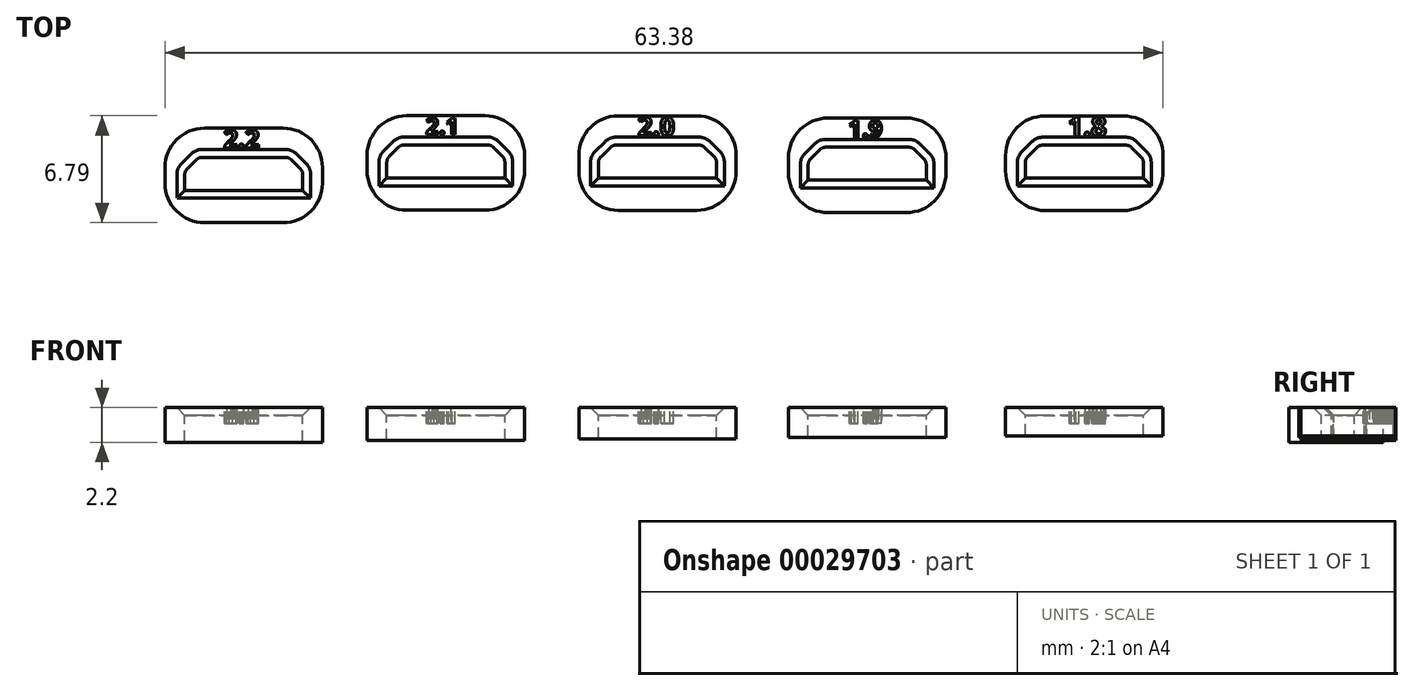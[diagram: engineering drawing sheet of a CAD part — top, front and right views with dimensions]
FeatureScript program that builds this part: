
annotation { "Feature Type Name" : "Feature", "Feature Type Description" : "" }
export const myFeature = defineFeature(function(context is Context, id is Id, definition is map)
    precondition{}
    {
        {
            var Q0;
            Q0=qCreatedBy(makeId("Top.planeOp"),FACE);
            var sketch = newSketch(context, id + "F0", { "sketchPlane" : qUnion([Q0])});
            skLineSegment(sketch, "E0", {"start": v(-1.37, -1.33) * mm, "end": v(6.13, -1.33) * mm});
            skLineSegment(sketch, "E1", {"start": v(6.13, -1.33) * mm, "end": v(6.13, -0.13) * mm});
            skLineSegment(sketch, "E2", {"start": v(6.13, -0.13) * mm, "end": v(5.23, 0.77) * mm});
            skLineSegment(sketch, "E3", {"start": v(5.23, 0.77) * mm, "end": v(-0.47, 0.77) * mm});
            skLineSegment(sketch, "E4", {"start": v(-0.47, 0.77) * mm, "end": v(-1.37, -0.13) * mm});
            skLineSegment(sketch, "E5", {"start": v(-1.37, -0.13) * mm, "end": v(-1.37, -1.33) * mm});
            skLineSegment(sketch, "E6.bottom", {"start": v(-2.62, 2.62) * mm, "end": v(7.38, 2.62) * mm});
            skLineSegment(sketch, "E6.top", {"start": v(-2.62, -3.38) * mm, "end": v(7.38, -3.38) * mm});
            skLineSegment(sketch, "E6.left", {"start": v(-2.62, 2.62) * mm, "end": v(-2.62, -3.38) * mm});
            skLineSegment(sketch, "E6.right", {"start": v(7.38, 2.62) * mm, "end": v(7.38, -3.38) * mm});
            skSolve(sketch);
        }
        {
            var Q0;
            Q0=makeQuery(id+"F0.imprint","IMPRINT",FACE,{"disambiguationData":[TD([[makeQuery(id+"F0.imprint","IMPRINT",EDGE,{"derivedFrom":sQuery(id+"F0.wireOp",EDGE,"E0")}),-1.0]])]});
            extrude(context, id + "F1", {"entities" : qUnion([Q0]), "oppositeDirection" : true, "depth" : 2.2 * mm});
        }
        {
            var Q0;
            Q0=qCreatedBy(makeId("Top.planeOp"),FACE);
            var sketch = newSketch(context, id + "F2", { "sketchPlane" : qUnion([Q0])});
            skLineSegment(sketch, "E7", {"start": v(11.46, -0.54) * mm, "end": v(18.96, -0.54) * mm});
            skLineSegment(sketch, "E8", {"start": v(18.96, -0.54) * mm, "end": v(18.96, 0.66) * mm});
            skLineSegment(sketch, "E9", {"start": v(18.96, 0.66) * mm, "end": v(18.06, 1.56) * mm});
            skLineSegment(sketch, "E10", {"start": v(18.06, 1.56) * mm, "end": v(12.36, 1.56) * mm});
            skLineSegment(sketch, "E11", {"start": v(12.36, 1.56) * mm, "end": v(11.46, 0.66) * mm});
            skLineSegment(sketch, "E12", {"start": v(11.46, 0.66) * mm, "end": v(11.46, -0.54) * mm});
            skLineSegment(sketch, "E13.bottom", {"start": v(10.2, 3.4) * mm, "end": v(20.2, 3.4) * mm});
            skLineSegment(sketch, "E13.top", {"start": v(10.2, -2.6) * mm, "end": v(20.2, -2.6) * mm});
            skLineSegment(sketch, "E13.left", {"start": v(10.2, 3.4) * mm, "end": v(10.2, -2.6) * mm});
            skLineSegment(sketch, "E13.right", {"start": v(20.2, 3.4) * mm, "end": v(20.2, -2.6) * mm});
            skLineSegment(sketch, "E14", {"start": v(24.9, -0.56) * mm, "end": v(32.4, -0.56) * mm});
            skLineSegment(sketch, "E15", {"start": v(32.4, -0.56) * mm, "end": v(32.4, 0.64) * mm});
            skLineSegment(sketch, "E16", {"start": v(32.4, 0.64) * mm, "end": v(31.5, 1.54) * mm});
            skLineSegment(sketch, "E17", {"start": v(31.5, 1.54) * mm, "end": v(25.8, 1.54) * mm});
            skLineSegment(sketch, "E18", {"start": v(25.8, 1.54) * mm, "end": v(24.9, 0.64) * mm});
            skLineSegment(sketch, "E19", {"start": v(24.9, 0.64) * mm, "end": v(24.9, -0.56) * mm});
            skLineSegment(sketch, "E20.bottom", {"start": v(23.65, 3.4) * mm, "end": v(33.65, 3.4) * mm});
            skLineSegment(sketch, "E20.top", {"start": v(23.65, -2.6) * mm, "end": v(33.65, -2.6) * mm});
            skLineSegment(sketch, "E20.left", {"start": v(23.65, 3.4) * mm, "end": v(23.65, -2.6) * mm});
            skLineSegment(sketch, "E20.right", {"start": v(33.65, 3.4) * mm, "end": v(33.65, -2.6) * mm});
            skLineSegment(sketch, "E21", {"start": v(38.22, -0.7) * mm, "end": v(45.72, -0.7) * mm});
            skLineSegment(sketch, "E22", {"start": v(45.72, -0.7) * mm, "end": v(45.72, 0.5) * mm});
            skLineSegment(sketch, "E23", {"start": v(45.72, 0.5) * mm, "end": v(44.82, 1.4) * mm});
            skLineSegment(sketch, "E24", {"start": v(44.82, 1.4) * mm, "end": v(39.12, 1.4) * mm});
            skLineSegment(sketch, "E25", {"start": v(39.12, 1.4) * mm, "end": v(38.22, 0.5) * mm});
            skLineSegment(sketch, "E26", {"start": v(38.22, 0.5) * mm, "end": v(38.22, -0.7) * mm});
            skLineSegment(sketch, "E27.bottom", {"start": v(36.97, 3.26) * mm, "end": v(46.97, 3.26) * mm});
            skLineSegment(sketch, "E27.top", {"start": v(36.97, -2.74) * mm, "end": v(46.97, -2.74) * mm});
            skLineSegment(sketch, "E27.left", {"start": v(36.97, 3.26) * mm, "end": v(36.97, -2.74) * mm});
            skLineSegment(sketch, "E27.right", {"start": v(46.97, 3.26) * mm, "end": v(46.97, -2.74) * mm});
            skLineSegment(sketch, "E28", {"start": v(52.01, -0.56) * mm, "end": v(59.51, -0.56) * mm});
            skLineSegment(sketch, "E29", {"start": v(59.51, -0.56) * mm, "end": v(59.51, 0.64) * mm});
            skLineSegment(sketch, "E30", {"start": v(59.51, 0.64) * mm, "end": v(58.61, 1.54) * mm});
            skLineSegment(sketch, "E31", {"start": v(58.61, 1.54) * mm, "end": v(52.91, 1.54) * mm});
            skLineSegment(sketch, "E32", {"start": v(52.91, 1.54) * mm, "end": v(52.01, 0.64) * mm});
            skLineSegment(sketch, "E33", {"start": v(52.01, 0.64) * mm, "end": v(52.01, -0.56) * mm});
            skLineSegment(sketch, "E34.bottom", {"start": v(50.76, 3.39) * mm, "end": v(60.76, 3.39) * mm});
            skLineSegment(sketch, "E34.top", {"start": v(50.76, -2.61) * mm, "end": v(60.76, -2.61) * mm});
            skLineSegment(sketch, "E34.left", {"start": v(50.76, 3.39) * mm, "end": v(50.76, -2.61) * mm});
            skLineSegment(sketch, "E34.right", {"start": v(60.76, 3.39) * mm, "end": v(60.76, -2.61) * mm});
            skSolve(sketch);
        }
        {
            var Q0;
            Q0=makeQuery(id+"F2.imprint","IMPRINT",FACE,{"disambiguationData":[TD([[makeQuery(id+"F2.imprint","IMPRINT",EDGE,{"derivedFrom":sQuery(id+"F2.wireOp",EDGE,"E7")}),-1.0]])]});
            extrude(context, id + "F3", {"entities" : qUnion([Q0]), "oppositeDirection" : true, "depth" : 2.1 * mm});
        }
        {
            var Q0;
            Q0=makeQuery(id+"F2.imprint","IMPRINT",FACE,{"disambiguationData":[TD([[makeQuery(id+"F2.imprint","IMPRINT",EDGE,{"derivedFrom":sQuery(id+"F2.wireOp",EDGE,"E14")}),-1.0]])]});
            extrude(context, id + "F4", {"entities" : qUnion([Q0]), "oppositeDirection" : true, "depth" : 2 * mm});
        }
        {
            var Q0;
            Q0=makeQuery(id+"F2.imprint","IMPRINT",FACE,{"disambiguationData":[TD([[makeQuery(id+"F2.imprint","IMPRINT",EDGE,{"derivedFrom":sQuery(id+"F2.wireOp",EDGE,"E21")}),-1.0]])]});
            extrude(context, id + "F5", {"entities" : qUnion([Q0]), "oppositeDirection" : true, "depth" : 1.9 * mm});
        }
        {
            var Q0;
            Q0=makeQuery(id+"F2.imprint","IMPRINT",FACE,{"disambiguationData":[TD([[makeQuery(id+"F2.imprint","IMPRINT",EDGE,{"derivedFrom":sQuery(id+"F2.wireOp",EDGE,"E28")}),-1.0]])]});
            extrude(context, id + "F6", {"entities" : qUnion([Q0]), "oppositeDirection" : true, "depth" : 1.8 * mm});
        }
        {
            var Q0;
            Q0=makeQuery(id+"F1.opExtrude","SWEPT_EDGE",EDGE,{"disambiguationData":[OSD([sQuery(id+"F0.wireOp",EDGE,"E6.top"),sQuery(id+"F0.wireOp",EDGE,"E6.left")])]});
            var Q1;
            Q1=makeQuery(id+"F1.opExtrude","SWEPT_EDGE",EDGE,{"disambiguationData":[OSD([sQuery(id+"F0.wireOp",EDGE,"E6.top"),sQuery(id+"F0.wireOp",EDGE,"E6.right")])]});
            var Q2;
            Q2=makeQuery(id+"F1.opExtrude","SWEPT_EDGE",EDGE,{"disambiguationData":[OSD([sQuery(id+"F0.wireOp",EDGE,"E6.bottom"),sQuery(id+"F0.wireOp",EDGE,"E6.right")])]});
            var Q3;
            Q3=makeQuery(id+"F1.opExtrude","SWEPT_EDGE",EDGE,{"disambiguationData":[OSD([sQuery(id+"F0.wireOp",EDGE,"E6.bottom"),sQuery(id+"F0.wireOp",EDGE,"E6.left")])]});
            var Q4;
            Q4=makeQuery(id+"F3.opExtrude","SWEPT_EDGE",EDGE,{"disambiguationData":[OSD([sQuery(id+"F2.wireOp",EDGE,"E13.top"),sQuery(id+"F2.wireOp",EDGE,"E13.left")])]});
            var Q5;
            Q5=makeQuery(id+"F3.opExtrude","SWEPT_EDGE",EDGE,{"disambiguationData":[OSD([sQuery(id+"F2.wireOp",EDGE,"E13.top"),sQuery(id+"F2.wireOp",EDGE,"E13.right")])]});
            var Q6;
            Q6=makeQuery(id+"F3.opExtrude","SWEPT_EDGE",EDGE,{"disambiguationData":[OSD([sQuery(id+"F2.wireOp",EDGE,"E13.bottom"),sQuery(id+"F2.wireOp",EDGE,"E13.right")])]});
            var Q7;
            Q7=makeQuery(id+"F3.opExtrude","SWEPT_EDGE",EDGE,{"disambiguationData":[OSD([sQuery(id+"F2.wireOp",EDGE,"E13.bottom"),sQuery(id+"F2.wireOp",EDGE,"E13.left")])]});
            var Q8;
            Q8=makeQuery(id+"F4.opExtrude","SWEPT_EDGE",EDGE,{"disambiguationData":[OSD([sQuery(id+"F2.wireOp",EDGE,"E20.top"),sQuery(id+"F2.wireOp",EDGE,"E20.left")])]});
            var Q9;
            Q9=makeQuery(id+"F4.opExtrude","SWEPT_EDGE",EDGE,{"disambiguationData":[OSD([sQuery(id+"F2.wireOp",EDGE,"E20.bottom"),sQuery(id+"F2.wireOp",EDGE,"E20.left")])]});
            var Q10;
            Q10=makeQuery(id+"F4.opExtrude","SWEPT_EDGE",EDGE,{"disambiguationData":[OSD([sQuery(id+"F2.wireOp",EDGE,"E20.top"),sQuery(id+"F2.wireOp",EDGE,"E20.right")])]});
            var Q11;
            Q11=makeQuery(id+"F4.opExtrude","SWEPT_EDGE",EDGE,{"disambiguationData":[OSD([sQuery(id+"F2.wireOp",EDGE,"E20.bottom"),sQuery(id+"F2.wireOp",EDGE,"E20.right")])]});
            var Q12;
            Q12=makeQuery(id+"F5.opExtrude","SWEPT_EDGE",EDGE,{"disambiguationData":[OSD([sQuery(id+"F2.wireOp",EDGE,"E27.top"),sQuery(id+"F2.wireOp",EDGE,"E27.left")])]});
            var Q13;
            Q13=makeQuery(id+"F5.opExtrude","SWEPT_EDGE",EDGE,{"disambiguationData":[OSD([sQuery(id+"F2.wireOp",EDGE,"E27.top"),sQuery(id+"F2.wireOp",EDGE,"E27.right")])]});
            var Q14;
            Q14=makeQuery(id+"F5.opExtrude","SWEPT_EDGE",EDGE,{"disambiguationData":[OSD([sQuery(id+"F2.wireOp",EDGE,"E27.bottom"),sQuery(id+"F2.wireOp",EDGE,"E27.right")])]});
            var Q15;
            Q15=makeQuery(id+"F5.opExtrude","SWEPT_EDGE",EDGE,{"disambiguationData":[OSD([sQuery(id+"F2.wireOp",EDGE,"E27.bottom"),sQuery(id+"F2.wireOp",EDGE,"E27.left")])]});
            var Q16;
            Q16=makeQuery(id+"F6.opExtrude","SWEPT_EDGE",EDGE,{"disambiguationData":[OSD([sQuery(id+"F2.wireOp",EDGE,"E34.top"),sQuery(id+"F2.wireOp",EDGE,"E34.left")])]});
            var Q17;
            Q17=makeQuery(id+"F6.opExtrude","SWEPT_EDGE",EDGE,{"disambiguationData":[OSD([sQuery(id+"F2.wireOp",EDGE,"E34.top"),sQuery(id+"F2.wireOp",EDGE,"E34.right")])]});
            var Q18;
            Q18=makeQuery(id+"F6.opExtrude","SWEPT_EDGE",EDGE,{"disambiguationData":[OSD([sQuery(id+"F2.wireOp",EDGE,"E34.bottom"),sQuery(id+"F2.wireOp",EDGE,"E34.left")])]});
            var Q19;
            Q19=makeQuery(id+"F6.opExtrude","SWEPT_EDGE",EDGE,{"disambiguationData":[OSD([sQuery(id+"F2.wireOp",EDGE,"E34.bottom"),sQuery(id+"F2.wireOp",EDGE,"E34.right")])]});
            fillet(context, id + "F7", {"entities" : qUnion([Q0, Q1, Q2, Q3, Q4, Q5, Q6, Q7, Q8, Q9, Q10, Q11, Q12, Q13, Q14, Q15, Q16, Q17, Q18, Q19]), "radius" : 2.5 * mm, "tangentPropagation" : true, "allowEdgeOverflow" : false});
        }
        {
            var Q0;
            Q0=makeQuery(id+"F1.opExtrude","SWEPT_EDGE",EDGE,{"disambiguationData":[OSD([sQuery(id+"F0.wireOp",EDGE,"E3"),sQuery(id+"F0.wireOp",EDGE,"E4")])]});
            var Q1;
            Q1=makeQuery(id+"F1.opExtrude","SWEPT_EDGE",EDGE,{"disambiguationData":[OSD([sQuery(id+"F0.wireOp",EDGE,"E4"),sQuery(id+"F0.wireOp",EDGE,"E5")])]});
            var Q2;
            Q2=makeQuery(id+"F1.opExtrude","SWEPT_EDGE",EDGE,{"disambiguationData":[OSD([sQuery(id+"F0.wireOp",EDGE,"E2"),sQuery(id+"F0.wireOp",EDGE,"E3")])]});
            var Q3;
            Q3=makeQuery(id+"F1.opExtrude","SWEPT_EDGE",EDGE,{"disambiguationData":[OSD([sQuery(id+"F0.wireOp",EDGE,"E1"),sQuery(id+"F0.wireOp",EDGE,"E2")])]});
            var Q4;
            Q4=makeQuery(id+"F3.opExtrude","SWEPT_EDGE",EDGE,{"disambiguationData":[OSD([sQuery(id+"F2.wireOp",EDGE,"E10"),sQuery(id+"F2.wireOp",EDGE,"E11")])]});
            var Q5;
            Q5=makeQuery(id+"F3.opExtrude","SWEPT_EDGE",EDGE,{"disambiguationData":[OSD([sQuery(id+"F2.wireOp",EDGE,"E11"),sQuery(id+"F2.wireOp",EDGE,"E12")])]});
            var Q6;
            Q6=makeQuery(id+"F3.opExtrude","SWEPT_EDGE",EDGE,{"disambiguationData":[OSD([sQuery(id+"F2.wireOp",EDGE,"E9"),sQuery(id+"F2.wireOp",EDGE,"E10")])]});
            var Q7;
            Q7=makeQuery(id+"F3.opExtrude","SWEPT_EDGE",EDGE,{"disambiguationData":[OSD([sQuery(id+"F2.wireOp",EDGE,"E8"),sQuery(id+"F2.wireOp",EDGE,"E9")])]});
            var Q8;
            Q8=makeQuery(id+"F4.opExtrude","SWEPT_EDGE",EDGE,{"disambiguationData":[OSD([sQuery(id+"F2.wireOp",EDGE,"E17"),sQuery(id+"F2.wireOp",EDGE,"E18")])]});
            var Q9;
            Q9=makeQuery(id+"F4.opExtrude","SWEPT_EDGE",EDGE,{"disambiguationData":[OSD([sQuery(id+"F2.wireOp",EDGE,"E16"),sQuery(id+"F2.wireOp",EDGE,"E17")])]});
            var Q10;
            Q10=makeQuery(id+"F4.opExtrude","SWEPT_EDGE",EDGE,{"disambiguationData":[OSD([sQuery(id+"F2.wireOp",EDGE,"E15"),sQuery(id+"F2.wireOp",EDGE,"E16")])]});
            var Q11;
            Q11=makeQuery(id+"F4.opExtrude","SWEPT_EDGE",EDGE,{"disambiguationData":[OSD([sQuery(id+"F2.wireOp",EDGE,"E18"),sQuery(id+"F2.wireOp",EDGE,"E19")])]});
            var Q12;
            Q12=makeQuery(id+"F5.opExtrude","SWEPT_EDGE",EDGE,{"disambiguationData":[OSD([sQuery(id+"F2.wireOp",EDGE,"E25"),sQuery(id+"F2.wireOp",EDGE,"E26")])]});
            var Q13;
            Q13=makeQuery(id+"F5.opExtrude","SWEPT_EDGE",EDGE,{"disambiguationData":[OSD([sQuery(id+"F2.wireOp",EDGE,"E24"),sQuery(id+"F2.wireOp",EDGE,"E25")])]});
            var Q14;
            Q14=makeQuery(id+"F5.opExtrude","SWEPT_EDGE",EDGE,{"disambiguationData":[OSD([sQuery(id+"F2.wireOp",EDGE,"E23"),sQuery(id+"F2.wireOp",EDGE,"E24")])]});
            var Q15;
            Q15=makeQuery(id+"F5.opExtrude","SWEPT_EDGE",EDGE,{"disambiguationData":[OSD([sQuery(id+"F2.wireOp",EDGE,"E22"),sQuery(id+"F2.wireOp",EDGE,"E23")])]});
            var Q16;
            Q16=makeQuery(id+"F6.opExtrude","SWEPT_EDGE",EDGE,{"disambiguationData":[OSD([sQuery(id+"F2.wireOp",EDGE,"E32"),sQuery(id+"F2.wireOp",EDGE,"E33")])]});
            var Q17;
            Q17=makeQuery(id+"F6.opExtrude","SWEPT_EDGE",EDGE,{"disambiguationData":[OSD([sQuery(id+"F2.wireOp",EDGE,"E31"),sQuery(id+"F2.wireOp",EDGE,"E32")])]});
            var Q18;
            Q18=makeQuery(id+"F6.opExtrude","SWEPT_EDGE",EDGE,{"disambiguationData":[OSD([sQuery(id+"F2.wireOp",EDGE,"E30"),sQuery(id+"F2.wireOp",EDGE,"E31")])]});
            var Q19;
            Q19=makeQuery(id+"F6.opExtrude","SWEPT_EDGE",EDGE,{"disambiguationData":[OSD([sQuery(id+"F2.wireOp",EDGE,"E29"),sQuery(id+"F2.wireOp",EDGE,"E30")])]});
            fillet(context, id + "F8", {"entities" : qUnion([Q0, Q1, Q2, Q3, Q4, Q5, Q6, Q7, Q8, Q9, Q10, Q11, Q12, Q13, Q14, Q15, Q16, Q17, Q18, Q19]), "radius" : 0.5 * mm, "tangentPropagation" : true, "allowEdgeOverflow" : false});
        }
        {
            var Q0;
            Q0=makeQuery(id+"F1.opExtrude","CAP_EDGE",EDGE,{"disambiguationData":[OSD([sQuery(id+"F0.wireOp",EDGE,"E5")])],"isStart":true});
            var Q1;
            Q1=makeQuery(id+"F1.opExtrude","CAP_EDGE",EDGE,{"disambiguationData":[OSD([sQuery(id+"F0.wireOp",EDGE,"E0")])],"isStart":true});
            var Q2;
            Q2=makeQuery(id+"F3.opExtrude","CAP_EDGE",EDGE,{"disambiguationData":[OSD([sQuery(id+"F2.wireOp",EDGE,"E10")])],"isStart":true});
            var Q3;
            Q3=makeQuery(id+"F3.opExtrude","CAP_EDGE",EDGE,{"disambiguationData":[OSD([sQuery(id+"F2.wireOp",EDGE,"E7")])],"isStart":true});
            var Q4;
            Q4=makeQuery(id+"F4.opExtrude","CAP_EDGE",EDGE,{"disambiguationData":[OSD([sQuery(id+"F2.wireOp",EDGE,"E17")])],"isStart":true});
            var Q5;
            Q5=makeQuery(id+"F4.opExtrude","CAP_EDGE",EDGE,{"disambiguationData":[OSD([sQuery(id+"F2.wireOp",EDGE,"E14")])],"isStart":true});
            var Q6;
            Q6=makeQuery(id+"F5.opExtrude","CAP_EDGE",EDGE,{"disambiguationData":[OSD([sQuery(id+"F2.wireOp",EDGE,"E24")])],"isStart":true});
            var Q7;
            Q7=makeQuery(id+"F5.opExtrude","CAP_EDGE",EDGE,{"disambiguationData":[OSD([sQuery(id+"F2.wireOp",EDGE,"E21")])],"isStart":true});
            var Q8;
            Q8=makeQuery(id+"F6.opExtrude","CAP_EDGE",EDGE,{"disambiguationData":[OSD([sQuery(id+"F2.wireOp",EDGE,"E31")])],"isStart":true});
            var Q9;
            Q9=makeQuery(id+"F6.opExtrude","CAP_EDGE",EDGE,{"disambiguationData":[OSD([sQuery(id+"F2.wireOp",EDGE,"E28")])],"isStart":true});
            chamfer(context, id + "F9", {"entities" : qUnion([Q0, Q1, Q2, Q3, Q4, Q5, Q6, Q7, Q8, Q9]), "width" : 0.5 * mm, "tangentPropagation" : true});
        }
        {
            var Q0;
            Q0=makeQuery(id+"F3.opExtrude","CAP_FACE",FACE,{"disambiguationData":[OSD([sQuery(id+"F2.wireOp",EDGE,"E7"),sQuery(id+"F2.wireOp",EDGE,"E8"),sQuery(id+"F2.wireOp",EDGE,"E9"),sQuery(id+"F2.wireOp",EDGE,"E10"),sQuery(id+"F2.wireOp",EDGE,"E11"),sQuery(id+"F2.wireOp",EDGE,"E12"),sQuery(id+"F2.wireOp",EDGE,"E13.bottom"),sQuery(id+"F2.wireOp",EDGE,"E13.top"),sQuery(id+"F2.wireOp",EDGE,"E13.left"),sQuery(id+"F2.wireOp",EDGE,"E13.right")])],"isStart":true});
            var sketch = newSketch(context, id + "F10", { "sketchPlane" : qUnion([Q0])});
            skText(sketch, "E35", { "text": "2.1", "fontName": "OpenSans-Bold.ttf"});
            const initialGuessF10  = {"E35": [0.01393, 0.00221, 1, 0, 0.00106]};
            skSetInitialGuess(sketch, initialGuessF10);
            skSolve(sketch);
        }
        {
            var Q0;
            Q0 = qSketchRegion(id + "F10", true);
            extrude(context, id + "F11", {"entities" : qUnion([Q0]), "operationType" : NewBodyOperationType.REMOVE, "oppositeDirection" : true, "depth" : 1 * mm});
        }
        {
            var Q0;
            Q0=makeQuery(id+"F1.opExtrude","CAP_FACE",FACE,{"disambiguationData":[OSD([sQuery(id+"F0.wireOp",EDGE,"E0"),sQuery(id+"F0.wireOp",EDGE,"E1"),sQuery(id+"F0.wireOp",EDGE,"E2"),sQuery(id+"F0.wireOp",EDGE,"E3"),sQuery(id+"F0.wireOp",EDGE,"E4"),sQuery(id+"F0.wireOp",EDGE,"E5"),sQuery(id+"F0.wireOp",EDGE,"E6.bottom"),sQuery(id+"F0.wireOp",EDGE,"E6.top"),sQuery(id+"F0.wireOp",EDGE,"E6.left"),sQuery(id+"F0.wireOp",EDGE,"E6.right")])],"isStart":true});
            var sketch = newSketch(context, id + "F12", { "sketchPlane" : qUnion([Q0])});
            skText(sketch, "E36", { "text": "2.2", "fontName": "OpenSans-Bold.ttf"});
            const initialGuessF12  = {"E36": [0.00109, 0.00136, 1, 0, 0.00115]};
            skSetInitialGuess(sketch, initialGuessF12);
            skSolve(sketch);
        }
        {
            var Q0;
            Q0 = qSketchRegion(id + "F12", true);
            extrude(context, id + "F13", {"entities" : qUnion([Q0]), "operationType" : NewBodyOperationType.REMOVE, "oppositeDirection" : true, "depth" : 1 * mm});
        }
        {
            var Q0;
            Q0=makeQuery(id+"F4.opExtrude","CAP_FACE",FACE,{"disambiguationData":[OSD([sQuery(id+"F2.wireOp",EDGE,"E14"),sQuery(id+"F2.wireOp",EDGE,"E15"),sQuery(id+"F2.wireOp",EDGE,"E16"),sQuery(id+"F2.wireOp",EDGE,"E17"),sQuery(id+"F2.wireOp",EDGE,"E18"),sQuery(id+"F2.wireOp",EDGE,"E19"),sQuery(id+"F2.wireOp",EDGE,"E20.bottom"),sQuery(id+"F2.wireOp",EDGE,"E20.top"),sQuery(id+"F2.wireOp",EDGE,"E20.left"),sQuery(id+"F2.wireOp",EDGE,"E20.right")])],"isStart":true});
            var sketch = newSketch(context, id + "F14", { "sketchPlane" : qUnion([Q0])});
            skText(sketch, "E37", { "text": "2.0", "fontName": "OpenSans-Bold.ttf"});
            const initialGuessF14  = {"E37": [0.0274, 0.00214, 1, 0, 0.00118]};
            skSetInitialGuess(sketch, initialGuessF14);
            skSolve(sketch);
        }
        {
            var Q0;
            Q0 = qSketchRegion(id + "F14", true);
            extrude(context, id + "F15", {"entities" : qUnion([Q0]), "operationType" : NewBodyOperationType.REMOVE, "oppositeDirection" : true, "depth" : 1 * mm});
        }
        {
            var Q0;
            Q0=makeQuery(id+"F5.opExtrude","CAP_FACE",FACE,{"disambiguationData":[OSD([sQuery(id+"F2.wireOp",EDGE,"E21"),sQuery(id+"F2.wireOp",EDGE,"E22"),sQuery(id+"F2.wireOp",EDGE,"E23"),sQuery(id+"F2.wireOp",EDGE,"E24"),sQuery(id+"F2.wireOp",EDGE,"E25"),sQuery(id+"F2.wireOp",EDGE,"E26"),sQuery(id+"F2.wireOp",EDGE,"E27.bottom"),sQuery(id+"F2.wireOp",EDGE,"E27.top"),sQuery(id+"F2.wireOp",EDGE,"E27.left"),sQuery(id+"F2.wireOp",EDGE,"E27.right")])],"isStart":true});
            var sketch = newSketch(context, id + "F16", { "sketchPlane" : qUnion([Q0])});
            skText(sketch, "E38", { "text": "1.9", "fontName": "OpenSans-Bold.ttf"});
            const initialGuessF16  = {"E38": [0.04077, 0.00203, 1, 0, 0.00109]};
            skSetInitialGuess(sketch, initialGuessF16);
            skSolve(sketch);
        }
        {
            var Q0;
            Q0 = qSketchRegion(id + "F16", true);
            extrude(context, id + "F17", {"entities" : qUnion([Q0]), "operationType" : NewBodyOperationType.REMOVE, "oppositeDirection" : true, "depth" : 1 * mm});
        }
        {
            var Q0;
            Q0=makeQuery(id+"F6.opExtrude","CAP_FACE",FACE,{"disambiguationData":[OSD([sQuery(id+"F2.wireOp",EDGE,"E28"),sQuery(id+"F2.wireOp",EDGE,"E29"),sQuery(id+"F2.wireOp",EDGE,"E30"),sQuery(id+"F2.wireOp",EDGE,"E31"),sQuery(id+"F2.wireOp",EDGE,"E32"),sQuery(id+"F2.wireOp",EDGE,"E33"),sQuery(id+"F2.wireOp",EDGE,"E34.bottom"),sQuery(id+"F2.wireOp",EDGE,"E34.top"),sQuery(id+"F2.wireOp",EDGE,"E34.left"),sQuery(id+"F2.wireOp",EDGE,"E34.right")])],"isStart":true});
            var sketch = newSketch(context, id + "F18", { "sketchPlane" : qUnion([Q0])});
            skText(sketch, "E39", { "text": "1.8", "fontName": "OpenSans-Bold.ttf"});
            const initialGuessF18  = {"E39": [0.05473, 0.0021, 1, 0, 0.00123]};
            skSetInitialGuess(sketch, initialGuessF18);
            skSolve(sketch);
        }
        {
            var Q0;
            Q0 = qSketchRegion(id + "F18", true);
            extrude(context, id + "F19", {"entities" : qUnion([Q0]), "operationType" : NewBodyOperationType.REMOVE, "oppositeDirection" : true, "depth" : 1 * mm});
        }
    });
